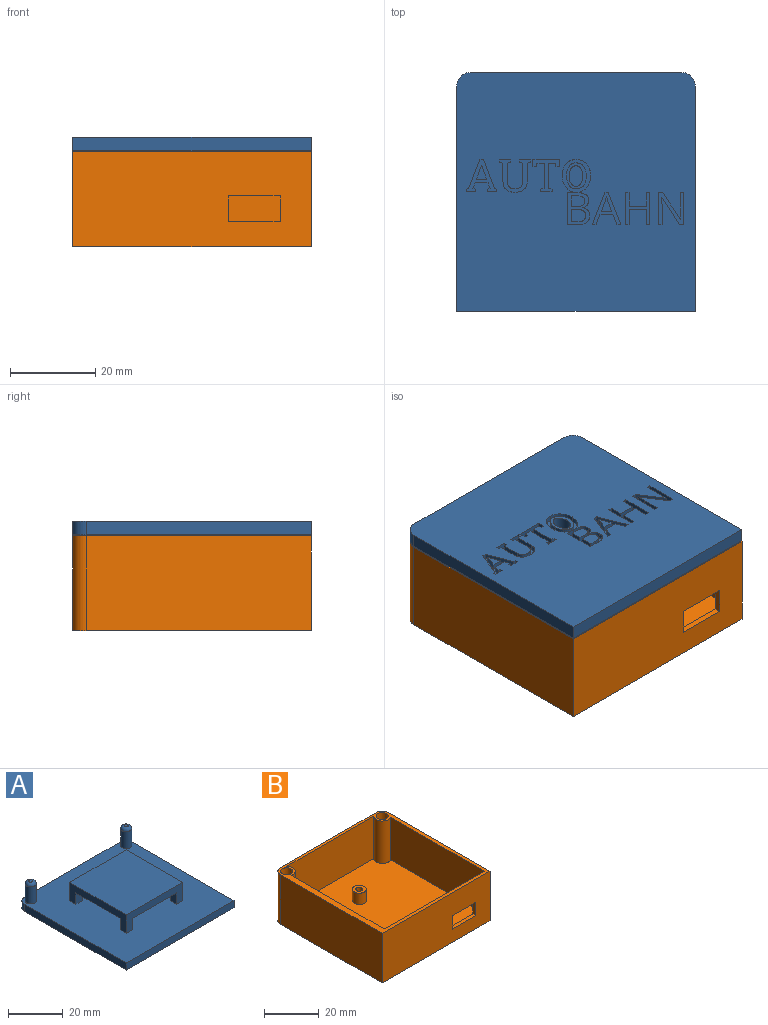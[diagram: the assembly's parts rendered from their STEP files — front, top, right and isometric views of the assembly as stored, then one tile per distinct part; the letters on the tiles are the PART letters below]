
ASSEMBLY  parts=2 mates=1
PART A: 185 faces, bbox 55.9x55.9x12.1 mm
  f0: plane 55.88x55.88mm, normal (0,0,-1), area 2931.6mm2, adj f1,f2,f3,f4,f12,f13,f14,f15
  f1: plane 52.71x3.18mm, normal (1,0,0), area 167.3mm2, adj f0,f4,f5,f12
  f2: plane 49.53x3.18mm, normal (0,1,0), area 157.3mm2, adj f0,f5,f12,f13
  f3: plane 52.71x3.18mm, normal (-1,0,0), area 167.3mm2, adj f0,f4,f5,f13
  f4: plane 55.88x3.18mm, normal (0,-1,0), area 177.4mm2, adj f0,f1,f3,f5
  f5: plane 55.88x55.88mm, normal (0,0,1), area 3039.5mm2, adj f1,f2,f3,f4,f6,f8,f12,f13
  f6: cylinder r=2.03mm len=7.62mm, axis (0,0,-1), area 97.3mm2, adj f5,f11
  f7: plane 1.52x1.52mm, normal (0,0,1), area 1.8mm2, adj f11
  f8: cylinder r=2.03mm len=7.62mm, axis (0,0,-1), area 97.3mm2, adj f5,f10
  f9: plane 1.52x1.52mm, normal (0,0,1), area 1.8mm2, adj f10
  f10: torus R=0.76mm, axis (0,0,1), area 19.7mm2, adj f8,f9
  f11: torus R=0.76mm, axis (0,0,1), area 19.7mm2, adj f6,f7
  f12: cylinder r=3.17mm len=3.18mm, axis (0,0,1), area 15.8mm2, adj f0,f1,f2,f5
  f13: cylinder r=3.17mm len=3.18mm, axis (0,0,-1), area 15.8mm2, adj f0,f2,f3,f5
  f14: plane 1.27x0.66mm, normal (1,0,0), area 0.8mm2, adj f0,f15,f35,f36
  f15: plane 2.7x1.27mm, normal (0,-1,0), area 3.4mm2, adj f0,f14,f16,f36
  f16: plane 1.27x0.66mm, normal (-1,0,0), area 0.8mm2, adj f0,f15,f17,f36
  f17: plane 1.27x0.84mm, normal (-0.17,0.99,0), area 1.1mm2, adj f0,f16,f18,f36
  f18: plane 4.3x1.27mm, normal (-1,0,0), area 5.5mm2, adj f0,f17,f19,f36
  f19: extruded ~1.88x1.27mm, area 2.7mm2, adj f0,f18,f20,f36
  f20: extruded ~2.02x1.27mm, area 2.7mm2, adj f0,f19,f21,f36
  f21: extruded ~2.08x1.27mm, area 2.8mm2, adj f0,f20,f22,f36
  f22: extruded ~1.88x1.27mm, area 2.7mm2, adj f0,f21,f23,f36
  f23: plane 4.3x1.27mm, normal (1,0,0), area 5.5mm2, adj f0,f22,f24,f36
  f24: plane 1.27x0.84mm, normal (0.17,0.99,0), area 1.1mm2, adj f0,f23,f25,f36
  f25: plane 1.27x0.66mm, normal (1,0,0), area 0.8mm2, adj f0,f24,f26,f36
  f26: plane 2.7x1.27mm, normal (0,-1,0), area 3.4mm2, adj f0,f25,f27,f36
  f27: plane 1.27x0.66mm, normal (-1,0,0), area 0.8mm2, adj f0,f26,f28,f36
  f28: plane 1.27x0.84mm, normal (-0.17,0.99,0), area 1.1mm2, adj f0,f27,f29,f36
  f29: plane 4.3x1.27mm, normal (-1,0,0), area 5.5mm2, adj f0,f28,f30,f36
  f30: extruded ~1.3x1.27mm, area 1.8mm2, adj f0,f29,f31,f36
  f31: extruded ~1.35x1.27mm, area 1.8mm2, adj f0,f30,f32,f36
  f32: extruded ~1.28x1.27mm, area 1.8mm2, adj f0,f31,f33,f36
  f33: extruded ~1.3x1.27mm, area 1.8mm2, adj f0,f32,f34,f36
  f34: plane 4.3x1.27mm, normal (1,0,0), area 5.5mm2, adj f0,f33,f35,f36
  f35: plane 1.27x0.84mm, normal (0.17,0.99,0), area 1.1mm2, adj f0,f14,f34,f36
  f36: plane 7.63x7.35mm, normal (0,0,-1), area 19.4mm2, adj f14,f15,f16,f17,f18,f19,f20,f21
  f37: extruded ~2.14x1.27mm, area 2.9mm2, adj f38,f56,f57,f166
  f38: plane 1.27x0.12mm, normal (-1,0,0), area 0.2mm2, adj f37,f39,f57,f166
  f39: extruded ~2.15x1.27mm, area 2.9mm2, adj f38,f40,f57,f166
  f40: extruded ~1.75x1.27mm, area 2.6mm2, adj f39,f41,f57,f166
  f41: extruded ~1.66x1.27mm, area 2.5mm2, adj f40,f42,f57,f166
  f42: extruded ~2.15x1.27mm, area 2.9mm2, adj f41,f43,f57,f166
  f43: plane 1.27x0.12mm, normal (1,0,0), area 0.2mm2, adj f42,f44,f57,f166
  f44: extruded ~2.14x1.27mm, area 2.9mm2, adj f43,f45,f57,f166
  f45: extruded ~1.66x1.27mm, area 2.5mm2, adj f44,f56,f57,f166
  f46: extruded ~2.73x1.27mm, area 3.8mm2, adj f0,f47,f55,f57
  f47: plane 1.27x0.11mm, normal (1,0,0), area 0.1mm2, adj f0,f46,f48,f57
  f48: extruded ~2.73x1.27mm, area 3.8mm2, adj f0,f47,f49,f57
  f49: extruded ~2.44x1.27mm, area 3.5mm2, adj f0,f48,f50,f57
  f50: extruded ~2.37x1.27mm, area 3.4mm2, adj f0,f49,f51,f57
  f51: extruded ~2.73x1.27mm, area 3.7mm2, adj f0,f50,f52,f57
  f52: plane 1.27x0.11mm, normal (-1,0,0), area 0.1mm2, adj f0,f51,f53,f57
  f53: extruded ~2.73x1.27mm, area 3.7mm2, adj f0,f52,f54,f57
  f54: extruded ~2.37x1.27mm, area 3.4mm2, adj f0,f53,f55,f57
  f55: extruded ~2.44x1.27mm, area 3.5mm2, adj f0,f46,f54,f57
  f56: extruded ~1.74x1.27mm, area 2.5mm2, adj f37,f45,f57,f166
  f57: plane 7.74x6.66mm, normal (0,0,-1), area 18.5mm2, adj f37,f38,f39,f40,f41,f42,f43,f44
  f58: plane 2.34x1.27mm, normal (-0.94,0.35,0), area 3.2mm2, adj f59,f70,f71,f167
  f59: plane 2.44x1.27mm, normal (0,-1,0), area 3.1mm2, adj f58,f60,f71,f167
  f60: plane 2.34x1.27mm, normal (0.94,0.35,0), area 3.2mm2, adj f59,f61,f71,f167
  f61: extruded ~1.27x1.09mm, area 1.4mm2, adj f60,f70,f71,f167
  f62: plane 2.4x1.27mm, normal (-0.93,0.36,0), area 3.3mm2, adj f0,f63,f69,f71
  f63: plane 1.27x0.91mm, normal (0,1,0), area 1.2mm2, adj f0,f62,f64,f71
  f64: plane 7.59x2.97mm, normal (0.93,-0.36,0), area 10.3mm2, adj f0,f63,f65,f71
  f65: plane 1.27x0.74mm, normal (0,-1,0), area 0.9mm2, adj f0,f64,f66,f71
  f66: plane 7.59x2.99mm, normal (-0.93,-0.37,0), area 10.4mm2, adj f0,f65,f67,f71
  f67: plane 1.27x0.89mm, normal (0,1,0), area 1.1mm2, adj f0,f66,f68,f71
  f68: plane 2.4x1.27mm, normal (0.93,0.36,0), area 3.3mm2, adj f0,f67,f69,f71
  f69: plane 3.03x1.27mm, normal (0,1,0), area 3.8mm2, adj f0,f62,f68,f71
  f70: extruded ~1.27x1.09mm, area 1.5mm2, adj f58,f61,f71,f167
  f71: plane 7.59x6.7mm, normal (0,0,-1), area 14.7mm2, adj f58,f59,f60,f61,f62,f63,f64,f65
  f72: plane 2.83x1.27mm, normal (1,0,0), area 3.6mm2, adj f73,f96,f97,f168
  f73: plane 1.51x1.27mm, normal (0,1,0), area 1.9mm2, adj f72,f74,f97,f168
  f74: extruded ~1.44x1.27mm, area 1.9mm2, adj f73,f75,f97,f168
  f75: extruded ~1.27x1.03mm, area 1.5mm2, adj f74,f76,f97,f168
  f76: extruded ~1.27x1.11mm, area 1.6mm2, adj f75,f77,f97,f168
  f77: extruded ~1.38x1.27mm, area 1.8mm2, adj f76,f96,f97,f168
  f78: plane 1.45x1.27mm, normal (0,-1,0), area 1.8mm2, adj f79,f94,f97,f98
  f79: plane 2.47x1.27mm, normal (1,0,0), area 3.1mm2, adj f78,f80,f97,f98
  f80: plane 1.29x1.27mm, normal (0,1,0), area 1.6mm2, adj f79,f81,f97,f98
  f81: extruded ~1.45x1.27mm, area 1.9mm2, adj f80,f82,f97,f98
  f82: extruded ~1.27x0.92mm, area 1.4mm2, adj f81,f83,f97,f98
  f83: extruded ~1.27x0.98mm, area 1.4mm2, adj f82,f94,f97,f98
  f84: plane 2.14x1.27mm, normal (0,-1,0), area 2.7mm2, adj f0,f85,f95,f97
  f85: plane 7.56x1.27mm, normal (-1,0,0), area 9.6mm2, adj f0,f84,f86,f97
  f86: plane 2.64x1.27mm, normal (0,1,0), area 3.3mm2, adj f0,f85,f87,f97
  f87: extruded ~1.92x1.27mm, area 2.6mm2, adj f0,f86,f88,f97
  f88: extruded ~1.58x1.27mm, area 2.3mm2, adj f0,f87,f89,f97
  f89: extruded ~1.81x1.72mm, area 3.5mm2, adj f0,f88,f90,f97
  f90: plane 1.27x0.05mm, normal (1,0,0), area 0.1mm2, adj f0,f89,f91,f97
  f91: extruded ~1.27x1.09mm, area 1.6mm2, adj f0,f90,f92,f97
  f92: extruded ~1.27x1.11mm, area 1.5mm2, adj f0,f91,f93,f97
  f93: extruded ~1.42x1.27mm, area 2.1mm2, adj f0,f92,f95,f97
  f94: extruded ~1.34x1.27mm, area 1.8mm2, adj f78,f83,f97,f98
  f95: extruded ~2.18x1.27mm, area 2.9mm2, adj f0,f84,f93,f97
  f96: plane 1.58x1.27mm, normal (0,-1,0), area 2mm2, adj f72,f77,f97,f168
  f97: plane 7.56x5.24mm, normal (0,0,-1), area 19.5mm2, adj f72,f73,f74,f75,f76,f77,f78,f79
  f98: plane 3.2x2.47mm, normal (0,0,-1), area 7.2mm2, adj f78,f79,f80,f81,f82,f83,f94
  f99: plane 1.66x1.27mm, normal (1,0,0), area 2.1mm2, adj f0,f100,f114,f115
  f100: plane 6.25x1.27mm, normal (0,-1,0), area 7.9mm2, adj f0,f99,f101,f115
  f101: plane 1.66x1.27mm, normal (-1,0,0), area 2.1mm2, adj f0,f100,f102,f115
  f102: plane 1.27x0.87mm, normal (0,1,0), area 1.1mm2, adj f0,f101,f103,f115
  f103: plane 1.27x0.86mm, normal (1,0.08,0), area 1.1mm2, adj f0,f102,f104,f115
  f104: plane 1.67x1.27mm, normal (0,1,0), area 2.1mm2, adj f0,f103,f105,f115
  f105: plane 5.93x1.27mm, normal (-1,0,0), area 7.5mm2, adj f0,f104,f106,f115
  f106: plane 1.27x0.84mm, normal (-0.17,-0.99,0), area 1.1mm2, adj f0,f105,f107,f115
  f107: plane 1.27x0.65mm, normal (-1,0,0), area 0.8mm2, adj f0,f106,f108,f115
  f108: plane 2.7x1.27mm, normal (0,1,0), area 3.4mm2, adj f0,f107,f109,f115
  f109: plane 1.27x0.65mm, normal (1,0,0), area 0.8mm2, adj f0,f108,f110,f115
  f110: plane 1.27x0.84mm, normal (0.17,-0.99,0), area 1.1mm2, adj f0,f109,f111,f115
  f111: plane 5.93x1.27mm, normal (1,0,0), area 7.5mm2, adj f0,f110,f112,f115
  f112: plane 1.67x1.27mm, normal (0,1,0), area 2.1mm2, adj f0,f111,f113,f115
  f113: plane 1.27x0.86mm, normal (-1,0.09,0), area 1.1mm2, adj f0,f112,f114,f115
  f114: plane 1.27x0.87mm, normal (0,1,0), area 1.1mm2, adj f0,f99,f113,f115
  f115: plane 7.52x6.25mm, normal (0,0,-1), area 14.6mm2, adj f99,f100,f101,f102,f103,f104,f105,f106
  f116: plane 1.27x0.88mm, normal (0,1,0), area 1.1mm2, adj f0,f117,f127,f128
  f117: plane 7.56x1.27mm, normal (1,0,0), area 9.6mm2, adj f0,f116,f118,f128
  f118: plane 1.27x0.88mm, normal (0,-1,0), area 1.1mm2, adj f0,f117,f119,f128
  f119: plane 3.21x1.27mm, normal (-1,0,0), area 4.1mm2, adj f0,f118,f120,f128
  f120: plane 3.98x1.27mm, normal (0,-1,0), area 5.1mm2, adj f0,f119,f121,f128
  f121: plane 3.21x1.27mm, normal (1,0,0), area 4.1mm2, adj f0,f120,f122,f128
  f122: plane 1.27x0.88mm, normal (0,-1,0), area 1.1mm2, adj f0,f121,f123,f128
  f123: plane 7.56x1.27mm, normal (-1,0,0), area 9.6mm2, adj f0,f122,f124,f128
  f124: plane 1.27x0.88mm, normal (0,1,0), area 1.1mm2, adj f0,f123,f125,f128
  f125: plane 3.56x1.27mm, normal (1,0,0), area 4.5mm2, adj f0,f124,f126,f128
  f126: plane 3.98x1.27mm, normal (0,1,0), area 5.1mm2, adj f0,f125,f127,f128
  f127: plane 3.56x1.27mm, normal (-1,0,0), area 4.5mm2, adj f0,f116,f126,f128
  f128: plane 7.56x5.74mm, normal (0,0,-1), area 16.4mm2, adj f116,f117,f118,f119,f120,f121,f122,f123
  f129: plane 1.27x1mm, normal (0,1,0), area 1.3mm2, adj f0,f130,f143,f144
  f130: plane 7.56x1.27mm, normal (1,0,0), area 9.6mm2, adj f0,f129,f131,f144
  f131: plane 1.27x0.82mm, normal (0,-1,0), area 1mm2, adj f0,f130,f132,f144
  f132: plane 4.34x1.27mm, normal (-1,0,0), area 5.5mm2, adj f0,f131,f133,f144
  f133: extruded ~1.27x1.08mm, area 1.4mm2, adj f0,f132,f134,f144
  f134: extruded ~1.27x0.9mm, area 1.1mm2, adj f0,f133,f135,f144
  f135: plane 1.27x0.04mm, normal (0,-1,0), area 0.1mm2, adj f0,f134,f136,f144
  f136: plane 6.32x4.12mm, normal (0.84,-0.55,0), area 9.6mm2, adj f0,f135,f137,f144
  f137: plane 1.27x0.99mm, normal (0,-1,0), area 1.3mm2, adj f0,f136,f138,f144
  f138: plane 7.56x1.27mm, normal (-1,0,0), area 9.6mm2, adj f0,f137,f139,f144
  f139: plane 1.27x0.81mm, normal (0,1,0), area 1mm2, adj f0,f138,f140,f144
  f140: plane 4.29x1.27mm, normal (1,0,0), area 5.5mm2, adj f0,f139,f141,f144
  f141: extruded ~2.05x1.27mm, area 2.6mm2, adj f0,f140,f142,f144
  f142: plane 1.27x0.04mm, normal (0,1,0), area 0.1mm2, adj f0,f141,f143,f144
  f143: plane 6.34x4.13mm, normal (-0.84,0.55,0), area 9.6mm2, adj f0,f129,f142,f144
  f144: plane 7.56x5.9mm, normal (0,0,-1), area 18.8mm2, adj f129,f130,f131,f132,f133,f134,f135,f136
  f145: plane 2.39x1.27mm, normal (0,-1,0), area 3mm2, adj f146,f164,f165,f169
  f146: plane 3.23x1.27mm, normal (0.94,0.35,0), area 4.4mm2, adj f145,f147,f165,f169
  f147: plane 1.27x0.03mm, normal (0,1,0), area 0mm2, adj f146,f164,f165,f169
  f148: plane 1.27x0.56mm, normal (-0.14,-0.99,0), area 0.7mm2, adj f0,f149,f163,f165
  f149: plane 1.27x0.65mm, normal (-1,0,0), area 0.8mm2, adj f0,f148,f150,f165
  f150: plane 2.15x1.27mm, normal (0,1,0), area 2.7mm2, adj f0,f149,f151,f165
  f151: plane 1.27x0.65mm, normal (1,0,0), area 0.8mm2, adj f0,f150,f152,f165
  f152: plane 1.27x0.57mm, normal (0.17,-0.99,0), area 0.7mm2, adj f0,f151,f153,f165
  f153: plane 1.39x1.27mm, normal (0.94,0.35,0), area 1.9mm2, adj f0,f152,f154,f165
  f154: plane 3.01x1.27mm, normal (0,1,0), area 3.8mm2, adj f0,f153,f155,f165
  f155: plane 1.39x1.27mm, normal (-0.94,0.34,0), area 1.9mm2, adj f0,f154,f156,f165
  f156: plane 1.27x0.57mm, normal (-0.17,-0.99,0), area 0.7mm2, adj f0,f155,f157,f165
  f157: plane 1.27x0.65mm, normal (-1,0,0), area 0.8mm2, adj f0,f156,f158,f165
  f158: plane 2.16x1.27mm, normal (0,1,0), area 2.7mm2, adj f0,f157,f159,f165
  f159: plane 1.27x0.65mm, normal (1,0,0), area 0.8mm2, adj f0,f158,f160,f165
  f160: plane 1.27x0.55mm, normal (0.14,-0.99,0), area 0.7mm2, adj f0,f159,f161,f165
  f161: plane 6.8x2.58mm, normal (0.93,-0.36,0), area 9.2mm2, adj f0,f160,f162,f165
  f162: plane 1.27x0.87mm, normal (0,-1,0), area 1.1mm2, adj f0,f161,f163,f165
  f163: plane 6.8x2.63mm, normal (-0.93,-0.36,0), area 9.3mm2, adj f0,f148,f162,f165
  f164: plane 3.23x1.27mm, normal (-0.94,0.34,0), area 4.4mm2, adj f145,f147,f165,f169
  f165: plane 7.52x7.2mm, normal (0,0,-1), area 17.9mm2, adj f145,f146,f147,f148,f149,f150,f151,f152
  f166: plane 6.07x4.62mm, normal (0,0,-1), area 10.4mm2, adj f37,f38,f39,f40,f41,f42,f43,f44
  f167: plane 3.43x2.44mm, normal (0,0,-1), area 4mm2, adj f58,f59,f60,f61,f70
  f168: plane 3.42x2.83mm, normal (0,0,-1), area 8.8mm2, adj f72,f73,f74,f75,f76,f77,f96
  f169: plane 3.23x2.39mm, normal (0,0,-1), area 3.9mm2, adj f145,f146,f147,f164
  f170: extruded ~4.86x3.28mm, area 40.9mm2, adj f5,f166
  f171: plane 29.21x8.26mm, normal (0,1,0), area 125mm2, adj f5,f172,f174,f175,f177,f183,f184
  f172: plane 29.21x8.26mm, normal (-1,0,0), area 125mm2, adj f5,f171,f173,f178,f180,f183,f184
  f173: plane 5.08x3.18mm, normal (0,-1,0), area 16.1mm2, adj f5,f172,f174,f183
  f174: plane 5.08x3.18mm, normal (1,0,0), area 16.1mm2, adj f5,f171,f173,f183
  f175: plane 5.08x3.18mm, normal (-1,0,0), area 16.1mm2, adj f5,f171,f176,f183
  f176: plane 5.08x3.18mm, normal (0,-1,0), area 16.1mm2, adj f5,f175,f177,f183
  f177: plane 29.21x8.26mm, normal (1,0,0), area 125mm2, adj f5,f171,f176,f178,f181,f183,f184
  f178: plane 29.21x8.26mm, normal (0,-1,0), area 125mm2, adj f5,f172,f177,f179,f182,f183,f184
  f179: plane 5.08x3.18mm, normal (1,0,0), area 16.1mm2, adj f5,f178,f180,f183
  f180: plane 5.08x3.18mm, normal (0,1,0), area 16.1mm2, adj f5,f172,f179,f183
  f181: plane 5.08x3.18mm, normal (0,1,0), area 16.1mm2, adj f5,f177,f182,f183
  f182: plane 5.08x3.18mm, normal (-1,0,0), area 16.1mm2, adj f5,f178,f181,f183
  f183: plane 29.21x29.21mm, normal (0,0,-1), area 812.9mm2, adj f171,f172,f173,f174,f175,f176,f177,f178
  f184: plane 29.21x29.21mm, normal (0,0,1), area 853.2mm2, adj f171,f172,f177,f178
PART B: 39 faces, bbox 55.9x55.9x22.2 mm
  f0: plane 55.88x22.23mm, normal (0,-1,0), area 1169.9mm2, adj f2,f4,f5,f15,f35,f36,f37,f38
  f1: plane 51.88x19.05mm, normal (0,1,0), area 916.2mm2, adj f8,f12,f15,f17,f35,f36,f37,f38
  f2: plane 52.71x22.23mm, normal (1,0,0), area 1171.4mm2, adj f0,f5,f7,f15
  f3: plane 49.53x22.23mm, normal (0,1,0), area 1100.8mm2, adj f5,f6,f7,f15
  f4: plane 52.71x22.23mm, normal (-1,0,0), area 1171.4mm2, adj f0,f5,f6,f15
  f5: plane 55.88x55.88mm, normal (0,0,-1), area 3118.2mm2, adj f0,f2,f3,f4,f6,f7
  f6: cylinder r=3.17mm len=22.23mm, axis (0,0,-1), area 110.8mm2, adj f3,f4,f5,f15
  f7: cylinder r=3.17mm len=22.23mm, axis (0,0,-1), area 110.8mm2, adj f2,f3,f5,f15
  f8: plane 48.1x19.05mm, normal (1,0,0), area 916.3mm2, adj f1,f9,f15,f17
  f9: cylinder r=3.17mm len=19.05mm, axis (0,0,-1), area 153.4mm2, adj f8,f10,f15,f17
  f10: plane 44.89x19.05mm, normal (0,-1,0), area 855.2mm2, adj f9,f11,f15,f17
  f11: cylinder r=3.17mm len=19.05mm, axis (0,0,-1), area 174.1mm2, adj f10,f12,f15,f17
  f12: plane 48.51x19.05mm, normal (-1,0,0), area 924.1mm2, adj f1,f11,f15,f17
  f13: cylinder r=2.22mm len=19.05mm, axis (0,0,-1), area 266mm2, adj f15,f16
  f14: cylinder r=2.22mm len=19.05mm, axis (0,0,-1), area 266mm2, adj f15,f18
  f15: plane 55.88x55.88mm, normal (0,0,1), area 359.1mm2, adj f0,f1,f2,f3,f4,f6,f7,f8
  f16: plane 4.45x4.45mm, normal (0,0,1), area 15.5mm2, adj f13
  f17: plane 53.37x51.88mm, normal (0,0,1), area 2647mm2, adj f1,f8,f9,f10,f11,f12,f20,f24
  f18: plane 4.45x4.45mm, normal (0,0,1), area 15.5mm2, adj f14
  f19: cylinder r=1.27mm len=5.08mm, axis (0,0,-1), area 40.5mm2, adj f21,f22
  f20: cylinder r=2.54mm len=5.08mm, axis (0,0,-1), area 81.1mm2, adj f17,f21
  f21: plane 5.08x5.08mm, normal (0,0,1), area 15.2mm2, adj f19,f20
  f22: plane 2.54x2.54mm, normal (0,0,1), area 5.1mm2, adj f19
  f23: cylinder r=1.27mm len=5.08mm, axis (0,0,-1), area 40.5mm2, adj f25,f26
  f24: cylinder r=2.54mm len=5.08mm, axis (0,0,-1), area 81.1mm2, adj f17,f25
  f25: plane 5.08x5.08mm, normal (0,0,1), area 15.2mm2, adj f23,f24
  f26: plane 2.54x2.54mm, normal (0,0,1), area 5.1mm2, adj f23
  f27: cylinder r=1.27mm len=5.08mm, axis (0,0,-1), area 40.5mm2, adj f29,f30
  f28: cylinder r=2.54mm len=5.08mm, axis (0,0,-1), area 81.1mm2, adj f17,f29
  f29: plane 5.08x5.08mm, normal (0,0,1), area 15.2mm2, adj f27,f28
  f30: plane 2.54x2.54mm, normal (0,0,1), area 5.1mm2, adj f27
  f31: cylinder r=1.27mm len=5.08mm, axis (0,0,-1), area 40.5mm2, adj f33,f34
  f32: cylinder r=2.54mm len=5.08mm, axis (0,0,-1), area 81.1mm2, adj f17,f33
  f33: plane 5.08x5.08mm, normal (0,0,1), area 15.2mm2, adj f31,f32
  f34: plane 2.54x2.54mm, normal (0,0,1), area 5.1mm2, adj f31
  f35: plane 12x1.5mm, normal (0,0,-1), area 18mm2, adj f0,f1,f36,f38
  f36: plane 6x1.5mm, normal (1,0,0), area 9mm2, adj f0,f1,f35,f37
  f37: plane 12x1.5mm, normal (0,0,1), area 18mm2, adj f0,f1,f36,f38
  f38: plane 6x1.5mm, normal (-1,0,0), area 9mm2, adj f0,f1,f35,f37
PLACE A rot(axis=(0,1,0),180deg) t=(-4.26,11,20.67)mm
PLACE B t=(-4.26,11,-4.98)mm fixed
MATE slider A.f6 <-> B.f7  axis (0,0,1) through (20.51,35.76,17.5)mm
